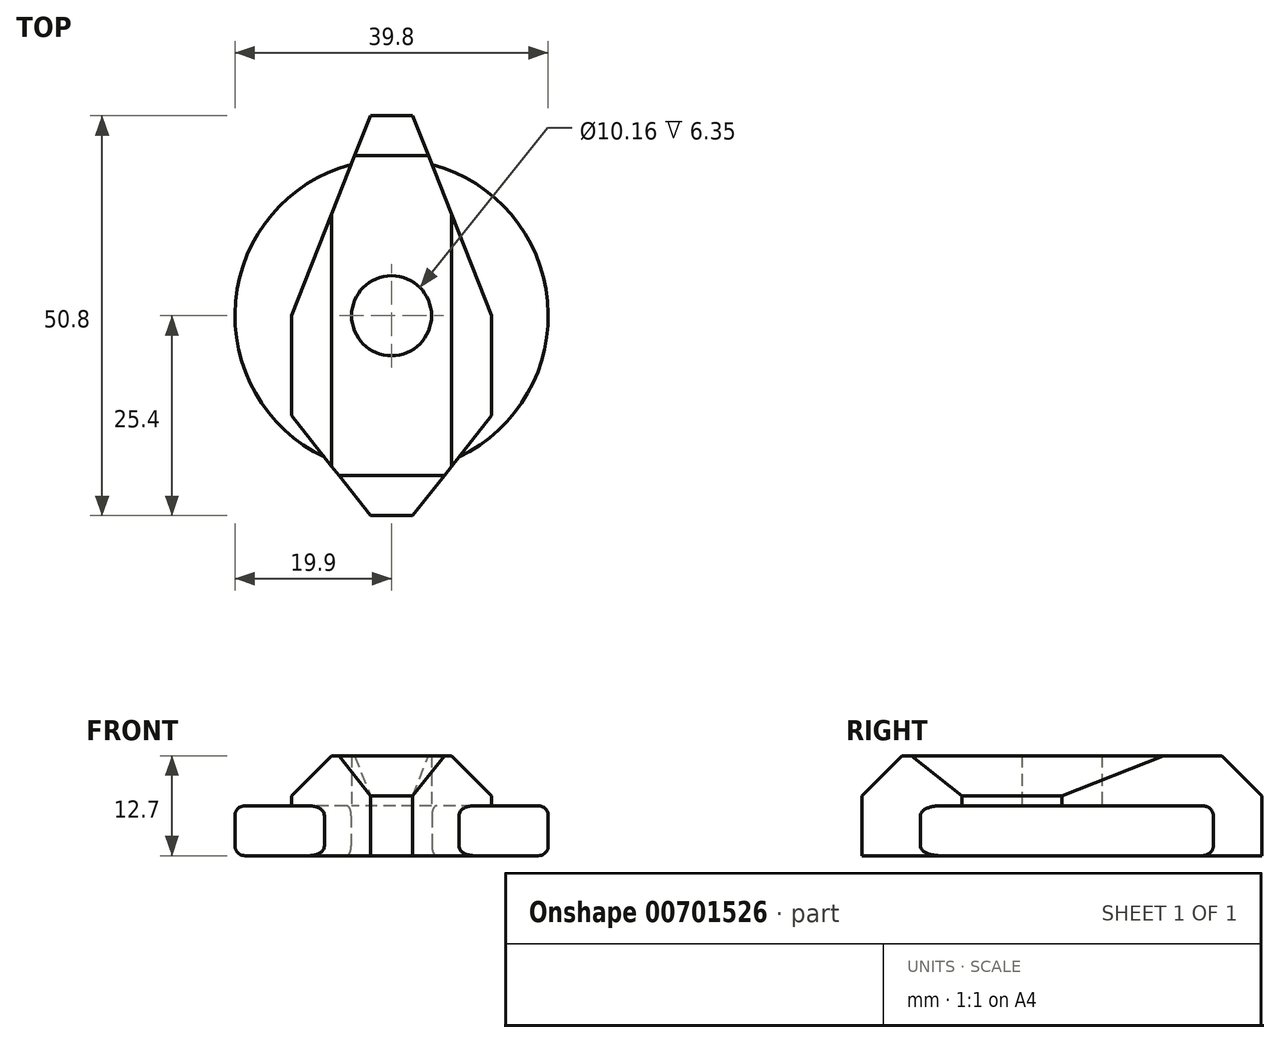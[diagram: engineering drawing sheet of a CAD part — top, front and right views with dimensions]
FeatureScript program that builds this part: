
annotation { "Feature Type Name" : "Feature", "Feature Type Description" : "" }
export const myFeature = defineFeature(function(context is Context, id is Id, definition is map)
    precondition{}
    {
        {
            var Q0;
            Q0=qCreatedBy(makeId("Top.planeOp"),FACE);
            var sketch = newSketch(context, id + "F0", { "sketchPlane" : qUnion([Q0])});
            skCircle(sketch, "E0", {"center": v(0, 0) * mm, "radius": 5.08 * mm});
            skLineSegment(sketch, "E1.bottom", {"start": v(12.7, 25.4) * mm, "end": v(-12.7, 25.4) * mm});
            skLineSegment(sketch, "E1.top", {"start": v(12.7, -25.4) * mm, "end": v(-12.7, -25.4) * mm});
            skLineSegment(sketch, "E1.left", {"start": v(12.7, 25.4) * mm, "end": v(12.7, -25.4) * mm});
            skLineSegment(sketch, "E1.right", {"start": v(-12.7, 25.4) * mm, "end": v(-12.7, -25.4) * mm});
            skSolve(sketch);
        }
        {
            var Q0;
            Q0 = qSketchRegion(id + "F0", true);
            extrude(context, id + "F1", {"entities" : qUnion([Q0]), "depth" : 12.7 * mm, "offsetDistance" : 25.4 * mm});
        }
        {
            var Q0;
            Q0=makeQuery(id+"F1.opExtrude","CAP_FACE",FACE,{"disambiguationData":[OSD([sQuery(id+"F0.wireOp",EDGE,"E0"),sQuery(id+"F0.wireOp",EDGE,"E1.bottom"),sQuery(id+"F0.wireOp",EDGE,"E1.top"),sQuery(id+"F0.wireOp",EDGE,"E1.left"),sQuery(id+"F0.wireOp",EDGE,"E1.right")])],"isStart":false});
            var sketch = newSketch(context, id + "F2", { "sketchPlane" : qUnion([Q0])});
            skLineSegment(sketch, "E2", {"start": v(-12.7, 0) * mm, "end": v(-2.7, 25.4) * mm});
            skLineSegment(sketch, "E3", {"start": v(-2.7, 25.4) * mm, "end": v(-12.7, 25.4) * mm});
            skLineSegment(sketch, "E4", {"start": v(-12.7, 0) * mm, "end": v(-12.7, 25.4) * mm});
            skLineSegment(sketch, "E5", {"start": v(-12.7, -12.7) * mm, "end": v(-2.7, -25.4) * mm});
            skLineSegment(sketch, "E6", {"start": v(-12.7, -12.7) * mm, "end": v(-12.7, -25.4) * mm});
            skLineSegment(sketch, "E7", {"start": v(-2.7, -25.4) * mm, "end": v(-12.7, -25.4) * mm});
            skLineSegment(sketch, "E8", {"start": v(2.7, -25.4) * mm, "end": v(12.7, -12.7) * mm});
            skLineSegment(sketch, "E9", {"start": v(12.7, -25.4) * mm, "end": v(2.7, -25.4) * mm});
            skLineSegment(sketch, "E10", {"start": v(12.7, -12.7) * mm, "end": v(12.7, -25.4) * mm});
            skLineSegment(sketch, "E11", {"start": v(2.7, 25.4) * mm, "end": v(12.7, 0) * mm});
            skLineSegment(sketch, "E12", {"start": v(12.7, 0) * mm, "end": v(12.7, 25.4) * mm});
            skLineSegment(sketch, "E13", {"start": v(2.7, 25.4) * mm, "end": v(12.7, 25.4) * mm});
            skSolve(sketch);
        }
        {
            var Q0;
            Q0 = qSketchRegion(id + "F2", true);
            extrude(context, id + "F3", {"entities" : qUnion([Q0]), "operationType" : NewBodyOperationType.REMOVE, "oppositeDirection" : true, "depth" : 25.4 * mm, "offsetDistance" : 25.4 * mm});
        }
        {
            var Q0;
            Q0=makeQuery(id+"F1.opExtrude","CAP_EDGE",EDGE,{"disambiguationData":[OSD([sQuery(id+"F0.wireOp",EDGE,"E1.right")])],"isStart":false});
            var Q1;
            Q1=makeQuery(id+"F1.opExtrude","CAP_EDGE",EDGE,{"disambiguationData":[OSD([sQuery(id+"F0.wireOp",EDGE,"E1.left")])],"isStart":false});
            var Q2;
            Q2=makeQuery(id+"F1.opExtrude","CAP_EDGE",EDGE,{"disambiguationData":[OSD([sQuery(id+"F0.wireOp",EDGE,"E1.top")])],"isStart":false});
            var Q3;
            Q3=makeQuery(id+"F3.boolean.opBoolean","COPY",EDGE,{"derivedFrom":makeQuery(id+"F3.opExtrude","CAP_EDGE",EDGE,{"disambiguationData":[OSD([sQuery(id+"F2.wireOp",EDGE,"E8")])],"isStart":true})});
            var Q4;
            Q4=makeQuery(id+"F3.boolean.opBoolean","COPY",EDGE,{"derivedFrom":makeQuery(id+"F3.opExtrude","CAP_EDGE",EDGE,{"disambiguationData":[OSD([sQuery(id+"F2.wireOp",EDGE,"E5")])],"isStart":true})});
            var Q5;
            Q5=makeQuery(id+"F3.boolean.opBoolean","COPY",EDGE,{"derivedFrom":makeQuery(id+"F3.opExtrude","CAP_EDGE",EDGE,{"disambiguationData":[OSD([sQuery(id+"F2.wireOp",EDGE,"E2")])],"isStart":true})});
            var Q6;
            Q6=makeQuery(id+"F3.boolean.opBoolean","COPY",EDGE,{"derivedFrom":makeQuery(id+"F3.opExtrude","CAP_EDGE",EDGE,{"disambiguationData":[OSD([sQuery(id+"F2.wireOp",EDGE,"E11")])],"isStart":true})});
            var Q7;
            Q7=makeQuery(id+"F1.opExtrude","CAP_EDGE",EDGE,{"disambiguationData":[OSD([sQuery(id+"F0.wireOp",EDGE,"E1.bottom")])],"isStart":false});
            chamfer(context, id + "F4", {"entities" : qUnion([Q0, Q1, Q2, Q3, Q4, Q5, Q6, Q7]), "width" : 5.08 * mm, "tangentPropagation" : true});
        }
        {
            var Q0;
            Q0=qCreatedBy(makeId("Top.planeOp"),FACE);
            var sketch = newSketch(context, id + "F5", { "sketchPlane" : qUnion([Q0])});
            skCircle(sketch, "E14", {"center": v(0, 0) * mm, "radius": 19.9 * mm});
            skSolve(sketch);
        }
        {
            var Q0;
            Q0 = qSketchRegion(id + "F5", true);
            extrude(context, id + "F6", {"entities" : qUnion([Q0]), "operationType" : NewBodyOperationType.ADD, "depth" : 6.35 * mm, "offsetDistance" : 25.4 * mm});
        }
        {
            var Q0;
            {var subQ0=sQuery(id+"F5.wireOp",EDGE,"E14");Q0=makeQuery(id+"F6.boolean.opBoolean","SPLIT",EDGE,{"disambiguationData":[TD([makeQuery(id+"F3.boolean.opBoolean","COPY",FACE,{"derivedFrom":makeQuery(id+"F3.opExtrude","SWEPT_FACE",FACE,{"disambiguationData":[OSD([sQuery(id+"F2.wireOp",EDGE,"E8")])]})})])],"derivedFrom":makeQuery(id+"F6.opExtrude","CAP_EDGE",EDGE,{"disambiguationData":[OSD([subQ0])],"isStart":true})});}
            var Q1;
            {var subQ0=sQuery(id+"F5.wireOp",EDGE,"E14");Q1=makeQuery(id+"F6.boolean.opBoolean","SPLIT",EDGE,{"disambiguationData":[TD([makeQuery(id+"F3.boolean.opBoolean","COPY",FACE,{"derivedFrom":makeQuery(id+"F3.opExtrude","SWEPT_FACE",FACE,{"disambiguationData":[OSD([sQuery(id+"F2.wireOp",EDGE,"E8")])]})})])],"derivedFrom":makeQuery(id+"F6.opExtrude","CAP_EDGE",EDGE,{"disambiguationData":[OSD([subQ0])],"isStart":false})});}
            var Q2;
            {var subQ0=sQuery(id+"F5.wireOp",EDGE,"E14");Q2=makeQuery(id+"F6.boolean.opBoolean","SPLIT",EDGE,{"disambiguationData":[TD([makeQuery(id+"F3.boolean.opBoolean","COPY",FACE,{"derivedFrom":makeQuery(id+"F3.opExtrude","SWEPT_FACE",FACE,{"disambiguationData":[OSD([sQuery(id+"F2.wireOp",EDGE,"E2")])]})})])],"derivedFrom":makeQuery(id+"F6.opExtrude","CAP_EDGE",EDGE,{"disambiguationData":[OSD([subQ0])],"isStart":false})});}
            var Q3;
            {var subQ0=sQuery(id+"F5.wireOp",EDGE,"E14");Q3=makeQuery(id+"F6.boolean.opBoolean","SPLIT",EDGE,{"disambiguationData":[TD([makeQuery(id+"F3.boolean.opBoolean","COPY",FACE,{"derivedFrom":makeQuery(id+"F3.opExtrude","SWEPT_FACE",FACE,{"disambiguationData":[OSD([sQuery(id+"F2.wireOp",EDGE,"E2")])]})})])],"derivedFrom":makeQuery(id+"F6.opExtrude","CAP_EDGE",EDGE,{"disambiguationData":[OSD([subQ0])],"isStart":true})});}
            fillet(context, id + "F7", {"entities" : qUnion([Q0, Q1, Q2, Q3]), "radius" : 1.27 * mm, "tangentPropagation" : true, "allowEdgeOverflow" : false});
        }
    });
